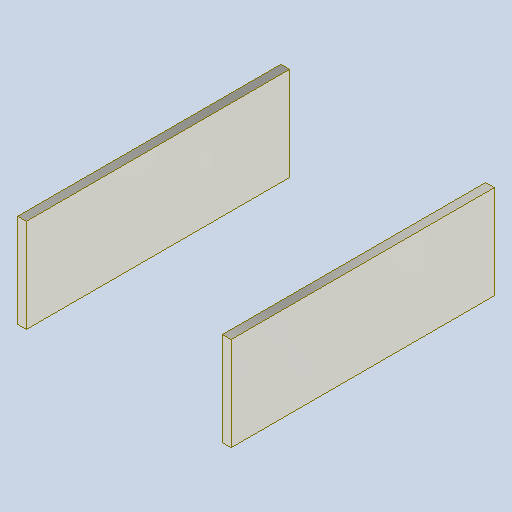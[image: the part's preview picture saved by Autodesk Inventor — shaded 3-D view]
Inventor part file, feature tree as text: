
AUTODESK INVENTOR PART (.ipt)
format: ipt  version: 2025.1 (Build 291241000, 241)  size: 219,648 bytes
history: native  units: mm
features: extrude x1, sketch x1
ambient origin geometry x8: Origin, YZ Plane, XZ Plane, XY Plane, X Axis, Y Axis, Z Axis, Center Point
bodies: Solid1 (feature_tree)
feature tree (2):
  extrude  "Extrusion1"  Depth=3.0mm
  sketch  "Sketch1"  dims[d0=73.0mm d1=3.0mm d2=32.0mm d3=16.0mm d5=0.0mm]
